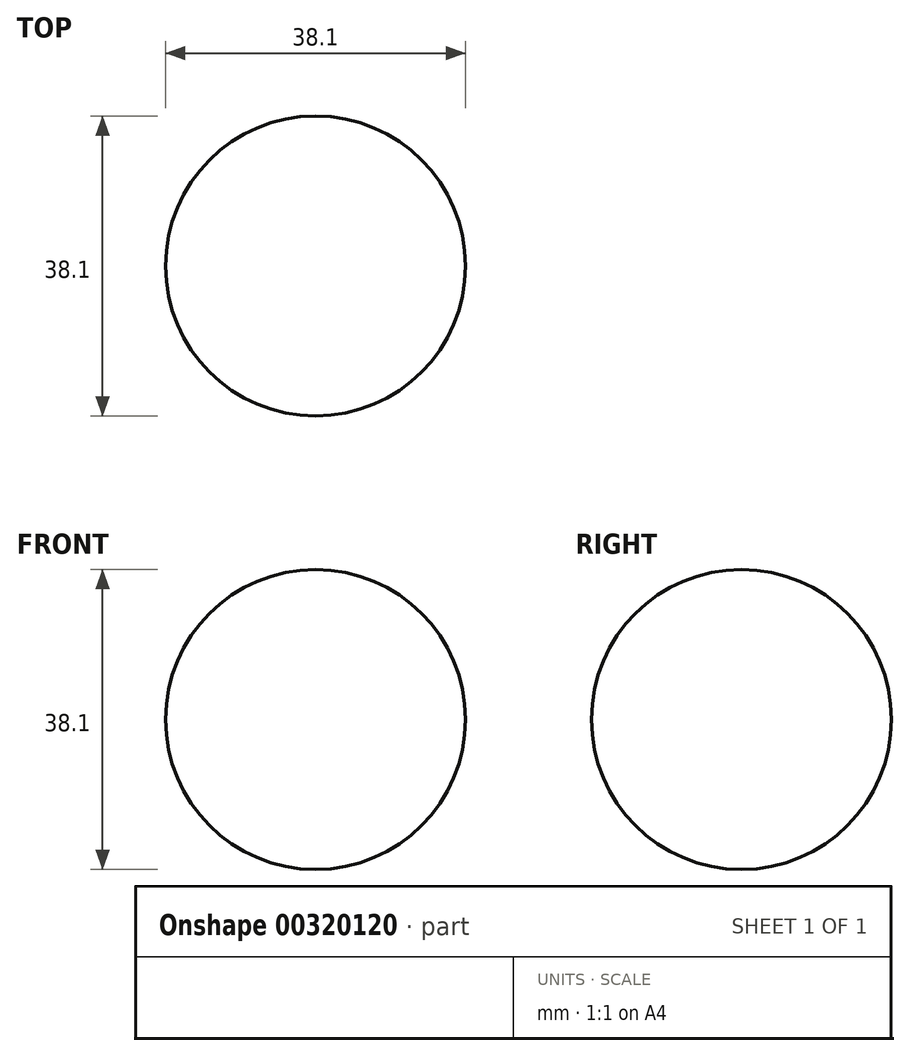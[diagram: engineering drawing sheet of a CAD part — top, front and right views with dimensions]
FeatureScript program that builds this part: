
annotation { "Feature Type Name" : "Feature", "Feature Type Description" : "" }
export const myFeature = defineFeature(function(context is Context, id is Id, definition is map)
    precondition{}
    {
        {
            var Q0;
            Q0=qCreatedBy(makeId("Front.planeOp"),FACE);
            var sketch = newSketch(context, id + "F0", { "sketchPlane" : qUnion([Q0])});
            skLineSegment(sketch, "E0", {"start": v(0, 27.14) * mm, "end": v(0, 65.24) * mm});
            skArc(sketch, "E1", {"start": v(0, 27.14) * mm, "mid": v(19.05, 46.19) * mm, "end": v(0, 65.24) * mm});
            skSolve(sketch);
        }
        {
            var Q0;
            Q0 = qSketchRegion(id + "F0", true);
            var Q1;
            Q1=sQuery(id+"F0.wireOp",EDGE,"E0");
            revolve(context, id + "F1", {"entities" : qUnion([Q0]), "axis" : qUnion([Q1]), "revolveType" : RevolveType.FULL});
        }
        {
            var Q0;
            Q0=qCreatedBy(makeId("Front.planeOp"),FACE);
            var sketch = newSketch(context, id + "F2", { "sketchPlane" : qUnion([Q0])});
            skLineSegment(sketch, "E2", {"start": v(0, 19.91) * mm, "end": v(0, 83.41) * mm});
            skArc(sketch, "E3", {"start": v(0, 19.91) * mm, "mid": v(31.75, 51.66) * mm, "end": v(0, 83.41) * mm});
            skSolve(sketch);
        }
        {
            var Q0;
            Q0 = qSketchRegion(id + "F2", true);
            var Q1;
            Q1=sQuery(id+"F2.wireOp",EDGE,"E3");
            var Q2;
            Q2=sQuery(id+"F2.wireOp",EDGE,"E2");
            revolve(context, id + "F3", {"bodyType" : ToolBodyType.SURFACE, "operationType" : NewBodyOperationType.ADD, "entities" : qUnion([Q0]), "surfaceEntities" : qUnion([Q1]), "axis" : qUnion([Q2]), "revolveType" : RevolveType.FULL});
        }
    });
